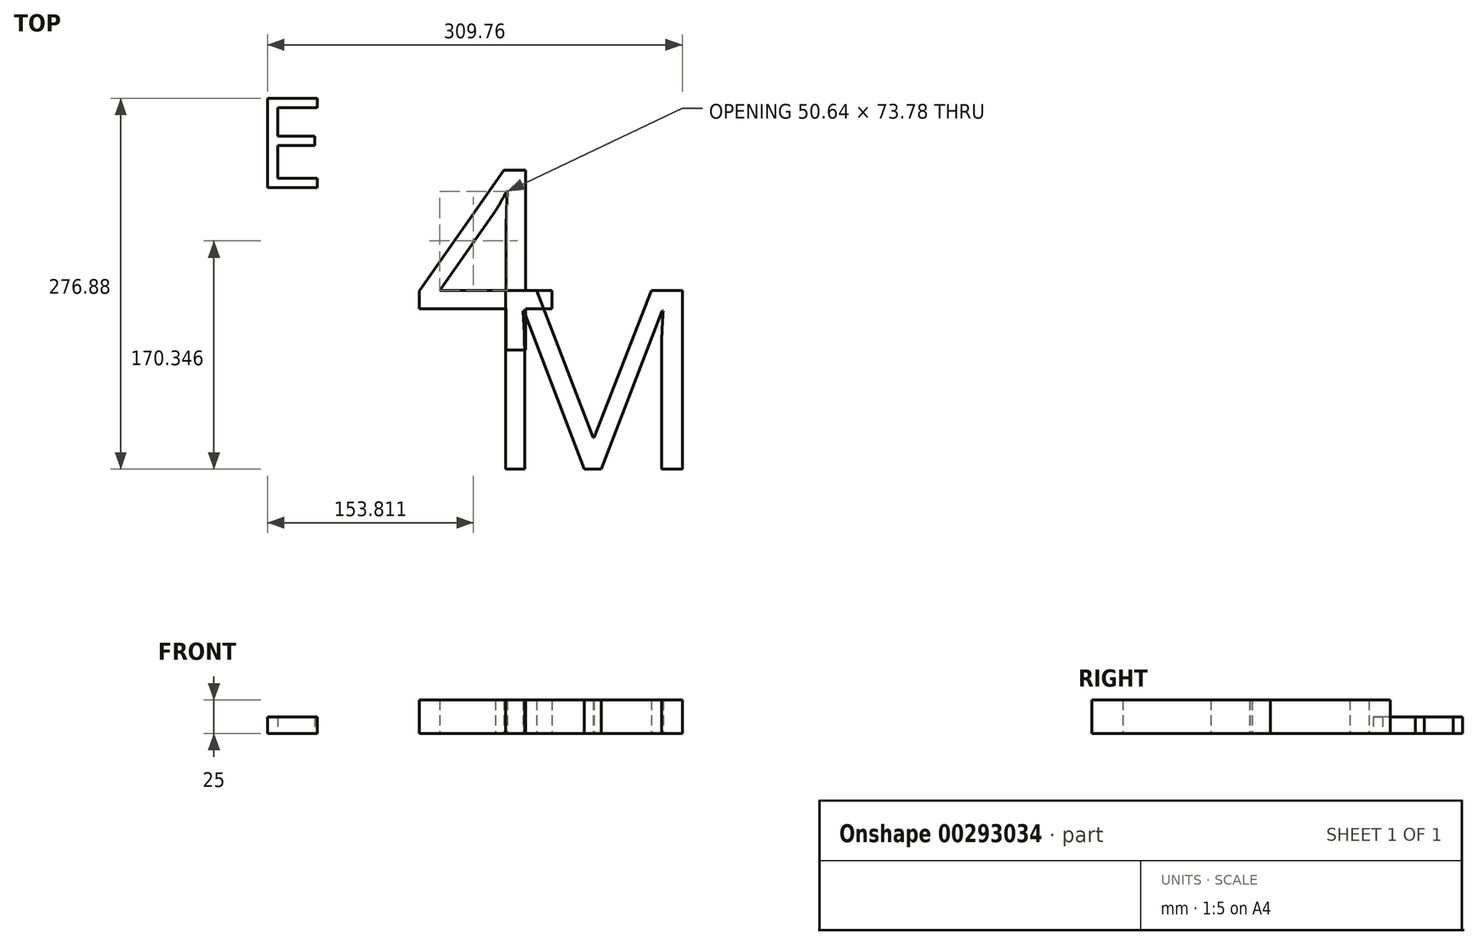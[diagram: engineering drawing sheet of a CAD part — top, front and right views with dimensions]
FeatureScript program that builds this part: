
annotation { "Feature Type Name" : "Feature", "Feature Type Description" : "" }
export const myFeature = defineFeature(function(context is Context, id is Id, definition is map)
    precondition{}
    {
        {
            var Q0;
            Q0=qCreatedBy(makeId("Top.planeOp"),FACE);
            var sketch = newSketch(context, id + "F0", { "sketchPlane" : qUnion([Q0])});
            skText(sketch, "E0", { "text": "E\n  4 \nM", "fontName": "OpenSans-Regular.ttf"});
            const initialGuessF0  = {"E0": [0.08905, -0.18027, 1, 0, 0.13449]};
            skSetInitialGuess(sketch, initialGuessF0);
            skSolve(sketch);
        }
        {
            var Q0;
            Q0 = qSketchRegion(id + "F0", true);
            extrude(context, id + "F1", {"entities" : qUnion([Q0]), "depth" : 25 * mm});
        }
        {
            var Q0;
            Q0=makeQuery(id+"F1.opExtrude","SWEPT_BODY",BODY,{"disambiguationData":[OSD([sQuery(id+"F0.wireOp",EDGE,"E0.sketch_text.stroke-12"),sQuery(id+"F0.wireOp",EDGE,"E0.sketch_text.stroke-13"),sQuery(id+"F0.wireOp",EDGE,"E0.sketch_text.stroke-14"),sQuery(id+"F0.wireOp",EDGE,"E0.sketch_text.stroke-15"),sQuery(id+"F0.wireOp",EDGE,"E0.sketch_text.stroke-16"),sQuery(id+"F0.wireOp",EDGE,"E0.sketch_text.stroke-17"),sQuery(id+"F0.wireOp",EDGE,"E0.sketch_text.stroke-18"),sQuery(id+"F0.wireOp",EDGE,"E0.sketch_text.stroke-19"),sQuery(id+"F0.wireOp",EDGE,"E0.sketch_text.stroke-20"),sQuery(id+"F0.wireOp",EDGE,"E0.sketch_text.stroke-21"),sQuery(id+"F0.wireOp",EDGE,"E0.sketch_text.stroke-22"),sQuery(id+"F0.wireOp",EDGE,"E0.sketch_text.stroke-23"),sQuery(id+"F0.wireOp",EDGE,"E0.sketch_text.stroke-24"),sQuery(id+"F0.wireOp",EDGE,"E0.sketch_text.stroke-25"),sQuery(id+"F0.wireOp",EDGE,"E0.sketch_text.stroke-26"),sQuery(id+"F0.wireOp",EDGE,"E0.sketch_text.stroke-27"),sQuery(id+"F0.wireOp",EDGE,"E0.sketch_text.stroke-28")])]});
            transform(context, id + "F2", {"entities" : qUnion([Q0]), "transformType" : TransformType.TRANSLATION_3D, "dx" : -23 * mm, "dy" : 223 * mm, "dz" : 0 * mm, "makeCopy" : false});
        }
        {
            var Q0;
            Q0=makeQuery(id+"F1.opExtrude","SWEPT_BODY",BODY,{"disambiguationData":[OSD([sQuery(id+"F0.wireOp",EDGE,"E0.sketch_text.stroke-29"),sQuery(id+"F0.wireOp",EDGE,"E0.sketch_text.stroke-30"),sQuery(id+"F0.wireOp",EDGE,"E0.sketch_text.stroke-31"),sQuery(id+"F0.wireOp",EDGE,"E0.sketch_text.stroke-32"),sQuery(id+"F0.wireOp",EDGE,"E0.sketch_text.stroke-33"),sQuery(id+"F0.wireOp",EDGE,"E0.sketch_text.stroke-34"),sQuery(id+"F0.wireOp",EDGE,"E0.sketch_text.stroke-35"),sQuery(id+"F0.wireOp",EDGE,"E0.sketch_text.stroke-36"),sQuery(id+"F0.wireOp",EDGE,"E0.sketch_text.stroke-37"),sQuery(id+"F0.wireOp",EDGE,"E0.sketch_text.stroke-38"),sQuery(id+"F0.wireOp",EDGE,"E0.sketch_text.stroke-39"),sQuery(id+"F0.wireOp",EDGE,"E0.sketch_text.stroke-40"),sQuery(id+"F0.wireOp",EDGE,"E0.sketch_text.stroke-41"),sQuery(id+"F0.wireOp",EDGE,"E0.sketch_text.stroke-42"),sQuery(id+"F0.wireOp",EDGE,"E0.sketch_text.stroke-43"),sQuery(id+"F0.wireOp",EDGE,"E0.sketch_text.stroke-44"),sQuery(id+"F0.wireOp",EDGE,"E0.sketch_text.stroke-45"),sQuery(id+"F0.wireOp",EDGE,"E0.sketch_text.stroke-46")])]});
            transform(context, id + "F3", {"entities" : qUnion([Q0]), "transformType" : TransformType.TRANSLATION_3D, "dx" : 124 * mm, "dy" : 388 * mm, "dz" : 0 * mm, "makeCopy" : false});
        }
        {
            var Q0;
            Q0=makeQuery(id+"F1.opExtrude","SWEPT_BODY",BODY,{"disambiguationData":[OSD([sQuery(id+"F0.wireOp",EDGE,"E0.sketch_text.stroke-0"),sQuery(id+"F0.wireOp",EDGE,"E0.sketch_text.stroke-1"),sQuery(id+"F0.wireOp",EDGE,"E0.sketch_text.stroke-2"),sQuery(id+"F0.wireOp",EDGE,"E0.sketch_text.stroke-3"),sQuery(id+"F0.wireOp",EDGE,"E0.sketch_text.stroke-4"),sQuery(id+"F0.wireOp",EDGE,"E0.sketch_text.stroke-5"),sQuery(id+"F0.wireOp",EDGE,"E0.sketch_text.stroke-6"),sQuery(id+"F0.wireOp",EDGE,"E0.sketch_text.stroke-7"),sQuery(id+"F0.wireOp",EDGE,"E0.sketch_text.stroke-8"),sQuery(id+"F0.wireOp",EDGE,"E0.sketch_text.stroke-9"),sQuery(id+"F0.wireOp",EDGE,"E0.sketch_text.stroke-10"),sQuery(id+"F0.wireOp",EDGE,"E0.sketch_text.stroke-11")])]});
            var Q1;
            Q1=qCreatedBy(makeId("Origin.pointOp"),VERTEX);
            transform(context, id + "F4", {"entities" : qUnion([Q0]), "transformType" : TransformType.SCALE_UNIFORMLY, "scale" : 0.5, "scalePoint" : qUnion([Q1]), "makeCopy" : false});
        }
    });
